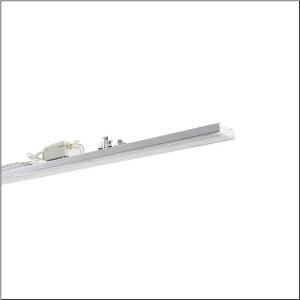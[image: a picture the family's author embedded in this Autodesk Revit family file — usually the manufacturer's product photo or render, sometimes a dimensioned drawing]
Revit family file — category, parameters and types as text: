
# Revit family: licross_r__21_recessed_ho_52tl18dn4e5m_39a1
name_source: partatom
category: Lighting Fixtures
units: mm (PartAtom-declared; Revit-internal decimal feet)

## family parameters
Cut with Voids When Loaded = No
Host = Face
Light Source = No
Part Type = Normal
Room Calculation Point = No
Round Connector Dimension = Use Diameter
Shared = No

## types (1)
- --- (1 x LED, 14850 lm, 84.6 W, 4000K)
    Apparent Load = 85 VA
    CIE Flux Codes = 75 94 99 100 100
    Color Rendering = 80
    Color Temperature = 4000K
    Default Elevation = 1800 mm
    Description = Licross® 21 Recessed HO, luminaire insert, of sheet steel, galvanised, coil coated, white, length: 1.500mm, width: 66mm, height: 67mm, LED rated luminous flux: 14.850lm, light colour: 840, control gear: DALI 2, with plug, 5-pole, with phase selection, mains connection: 220..240V, AC, 50/60Hz, rated input power: 85W, halogen-free wiring, primary light control with lens, of plastic, primary optical cover: cover, of PMMA, light emission: direct distribution, primary light characteristic: symmetric, protection rating (complete): IP40, insulation class (complete): insulation class I (protective earthing), certification: CE, ENEC, VDE, UKCA, protection symbol: D if used in an environment without relevant dust loads with corresponding accessories, impact resistance: IK06, permissible ambient temperature for indoor applications: -25..+30°C, corresponds to IFS (International Featured Standards) requirements for safety and quality in the food industry, reducing of maximum allowable ambient temperature of 5°C with ceiling mounting, LABS conformity tested according to VDMA 24364:2018-05, packaging unit: 1 piece
    Height = 58 mm
    Lamp = 1 x LED
    Lamp Light Flux = 14850 lm
    Lamp Power = 84.6 W
    Lamp count = 1
    Length = 1500 mm
    Luminous efficacy = 176 lm/W
    Manufacturer = Siteco
    ModVariant = No
    Model = 52TL18DN4E5M
    Mounting Place = Ceiling
    Mounting Type = Pendant
    Number of Poles = 1
    OnlyDefault = Yes
    Power Factor = 1
    Product Name = Licross® 21 Recessed HO
    Product group = luminaire insert
    ProductGroupID = 901
    Protection Class = Protection class I
    Protection Degree = IP 40
    RLX_Detail_Level = 1
    RLX_Emergency_Light_Flux = 0 lm
    RLX_Emergency_Type = 0
    RLX_Emergency_Type_DB = No
    RlxData = <blob elided: 24709 chars, md5=dfbf8020>
    Socket = socket
    Standby Power = 0 W
    System Light Flux = 14850 lm
    System Power = 85 W
    Type Comments = factory setting: luminous flux: 100 % | dim-lin: 254 | 484 mA
    Type Image = l_1296930.jpg
    URL = http://relux.com
    VarID = @adj_057287
    Voltage = 0 V
    Weight = 0.00 kg
    Width = 66 mm

## geometry (parser evidence)
native form markers: Blend x4, Sweep x14
no freeform markers — native parametric forms only
